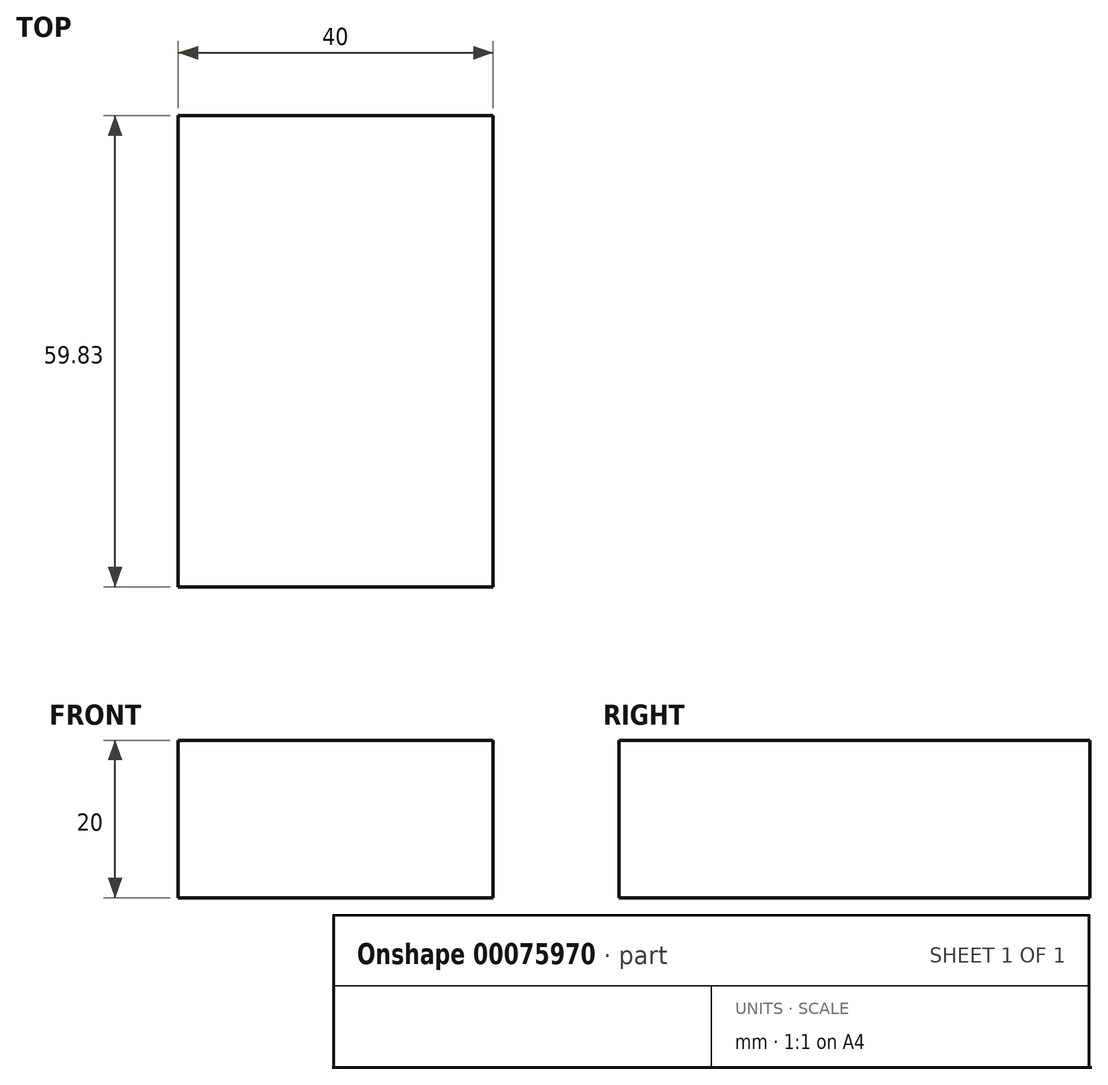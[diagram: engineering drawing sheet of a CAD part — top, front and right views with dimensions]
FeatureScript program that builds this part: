
annotation { "Feature Type Name" : "Feature", "Feature Type Description" : "" }
export const myFeature = defineFeature(function(context is Context, id is Id, definition is map)
    precondition{}
    {
        {
            var Q0;
            Q0=qCreatedBy(makeId("Front.planeOp"),FACE);
            var sketch = newSketch(context, id + "F0", { "sketchPlane" : qUnion([Q0])});
            skLineSegment(sketch, "E0.bottom", {"start": v(-40, 20) * mm, "end": v(0, 20) * mm});
            skLineSegment(sketch, "E0.top", {"start": v(-40, 0) * mm, "end": v(0, 0) * mm});
            skLineSegment(sketch, "E0.left", {"start": v(-40, 20) * mm, "end": v(-40, 0) * mm});
            skLineSegment(sketch, "E0.right", {"start": v(0, 20) * mm, "end": v(0, 0) * mm});
            skSolve(sketch);
        }
        {
            var Q0;
            Q0 = qSketchRegion(id + "F0", true);
            var Q1;
            Q1=makeQuery(id+"F0.imprint","IMPRINT",FACE,{"disambiguationData":[TD([[makeQuery(id+"F0.imprint","IMPRINT",EDGE,{"derivedFrom":sQuery(id+"F0.wireOp",EDGE,"E0.bottom")}),-1.0]])]});
            extrude(context, id + "F1", {"entities" : qUnion([Q0, Q1]), "depth" : 59.83 * mm});
        }
    });
